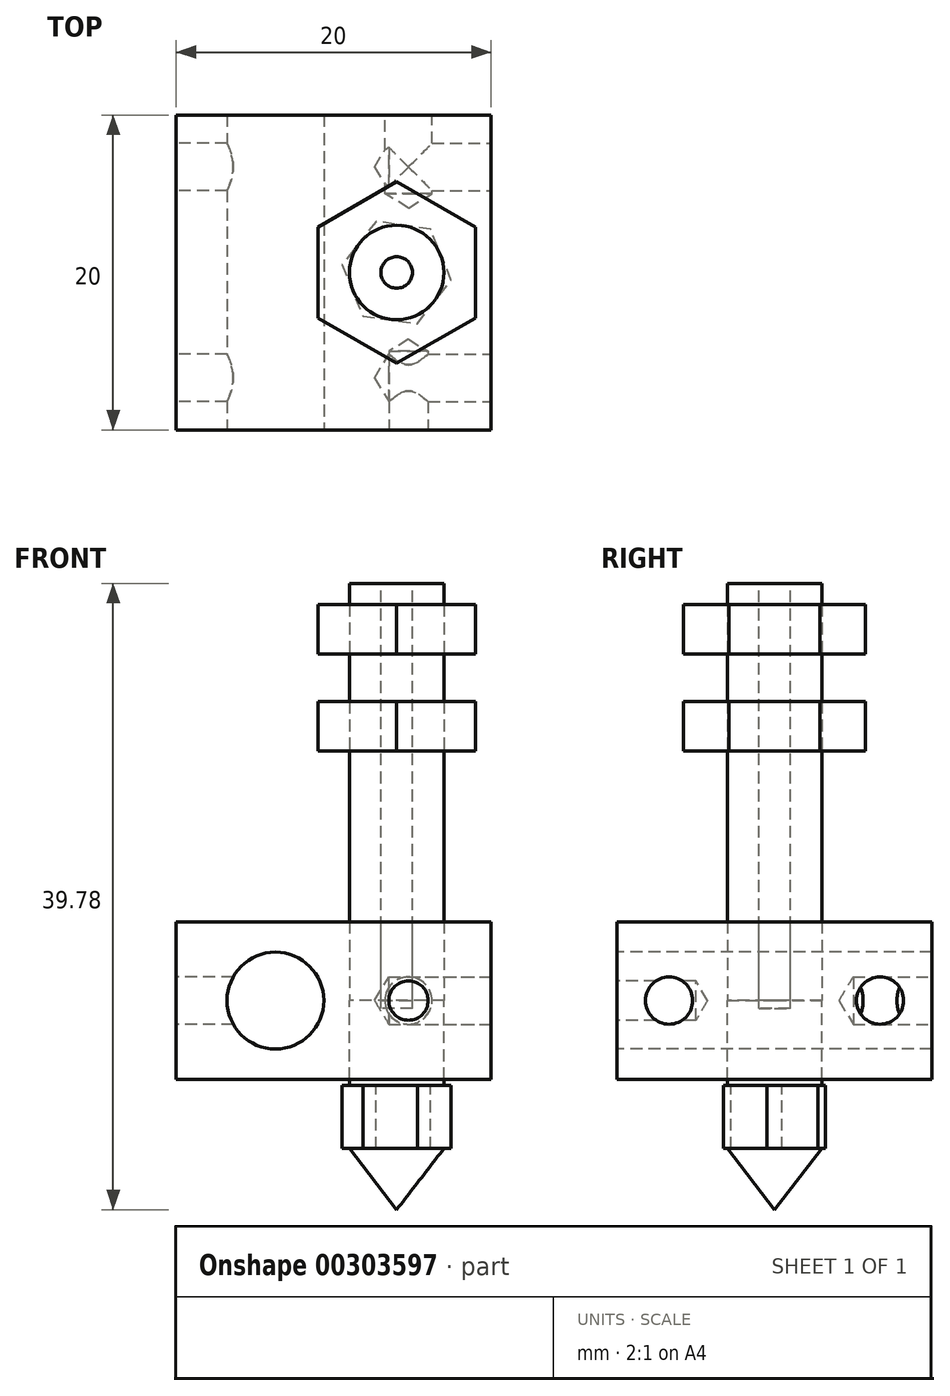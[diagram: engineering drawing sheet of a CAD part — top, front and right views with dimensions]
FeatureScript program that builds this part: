
annotation { "Feature Type Name" : "Feature", "Feature Type Description" : "" }
export const myFeature = defineFeature(function(context is Context, id is Id, definition is map)
    precondition{}
    {
        {
            var Q0;
            Q0=qCreatedBy(makeId("Top.planeOp"),FACE);
            var sketch = newSketch(context, id + "F0", { "sketchPlane" : qUnion([Q0])});
            skCircle(sketch, "E0", {"center": v(0, 0) * mm, "radius": 3 * mm});
            skSolve(sketch);
        }
        {
            var Q0;
            Q0 = qSketchRegion(id + "F0", true);
            extrude(context, id + "F1", {"entities" : qUnion([Q0]), "depth" : 26.5 * mm});
        }
        {
            var Q0;
            Q0=makeQuery(id+"F1.opExtrude","CAP_FACE",FACE,{"disambiguationData":[OSD([sQuery(id+"F0.wireOp",EDGE,"E0")])],"isStart":true});
            var sketch = newSketch(context, id + "F2", { "sketchPlane" : qUnion([Q0])});
            skCircle(sketch, "E1", {"center": v(0, 0) * mm, "radius": 3 * mm});
            skSolve(sketch);
        }
        {
            var Q0;
            Q0 = qSketchRegion(id + "F2", true);
            extrude(context, id + "F3", {"entities" : qUnion([Q0]), "depth" : 5.4 * mm});
        }
        {
            var Q0;
            Q0=makeQuery(id+"F3.opExtrude","CAP_FACE",FACE,{"disambiguationData":[OSD([sQuery(id+"F2.wireOp",EDGE,"E1")])],"isStart":false});
            var sketch = newSketch(context, id + "F4", { "sketchPlane" : qUnion([Q0])});
            skLineSegment(sketch, "E2.0", {"start": v(2.15, -2.76) * mm, "end": v(-1.31, -3.24) * mm});
            skLineSegment(sketch, "E2.1", {"start": v(-1.31, -3.24) * mm, "end": v(-3.46, -0.48) * mm});
            skLineSegment(sketch, "E2.2", {"start": v(-3.46, -0.48) * mm, "end": v(-2.15, 2.76) * mm});
            skLineSegment(sketch, "E2.3", {"start": v(-2.15, 2.76) * mm, "end": v(1.31, 3.24) * mm});
            skLineSegment(sketch, "E2.4", {"start": v(1.31, 3.24) * mm, "end": v(3.46, 0.48) * mm});
            skLineSegment(sketch, "E2.5", {"start": v(3.46, 0.48) * mm, "end": v(2.15, -2.76) * mm});
            skPoint(sketch, "E2.0.midPoint", {"position": v(0.42, -3) * mm});
            skPoint(sketch, "E2.cCircle.center.orphan", {"position": v(0, 0) * mm});
            skSolve(sketch);
        }
        {
            var Q0;
            Q0 = qSketchRegion(id + "F4", true);
            extrude(context, id + "F5", {"entities" : qUnion([Q0]), "operationType" : NewBodyOperationType.ADD, "depth" : 4 * mm});
        }
        {
            var Q0;
            Q0=qCreatedBy(makeId("Front.planeOp"),FACE);
            var sketch = newSketch(context, id + "F6", { "sketchPlane" : qUnion([Q0])});
            skLineSegment(sketch, "E3", {"start": v(0, -9.38) * mm, "end": v(0, -13.28) * mm});
            skLineSegment(sketch, "E4", {"start": v(0, -9.38) * mm, "end": v(-3.01, -9.38) * mm});
            skLineSegment(sketch, "E5", {"start": v(-3.01, -9.38) * mm, "end": v(0, -13.28) * mm});
            skSolve(sketch);
        }
        {
            var Q0;
            Q0 = qSketchRegion(id + "F6", true);
            var Q1;
            Q1=makeQuery(id+"F3.opExtrude","SWEPT_FACE",FACE,{"disambiguationData":[OSD([sQuery(id+"F2.wireOp",EDGE,"E1")])]});
            revolve(context, id + "F7", {"operationType" : NewBodyOperationType.ADD, "entities" : qUnion([Q0]), "axis" : qUnion([Q1]), "revolveType" : RevolveType.FULL});
        }
        {
            var Q0;
            Q0=qCreatedBy(makeId("Top.planeOp"),FACE);
            var sketch = newSketch(context, id + "F8", { "sketchPlane" : qUnion([Q0])});
            skLineSegment(sketch, "E6.bottom", {"start": v(-14, 10) * mm, "end": v(6, 10) * mm});
            skLineSegment(sketch, "E6.top", {"start": v(-14, -10) * mm, "end": v(6, -10) * mm});
            skLineSegment(sketch, "E6.left", {"start": v(-14, 10) * mm, "end": v(-14, -10) * mm});
            skLineSegment(sketch, "E6.right", {"start": v(6, 10) * mm, "end": v(6, -10) * mm});
            skSolve(sketch);
        }
        {
            var Q0;
            Q0 = qSketchRegion(id + "F8", true);
            extrude(context, id + "F9", {"entities" : qUnion([Q0]), "endBound" : BoundingType.SYMMETRIC, "depth" : 10 * mm});
        }
        {
            var Q0;
            Q0=makeQuery(id+"F9.opExtrude","SWEPT_FACE",FACE,{"disambiguationData":[OSD([sQuery(id+"F8.wireOp",EDGE,"E6.top")])]});
            var sketch = newSketch(context, id + "F10", { "sketchPlane" : qUnion([Q0])});
            skPoint(sketch, "E7", {"position": v(0.75, 0) * mm});
            skPoint(sketch, "E8", {"position": v(-7.7, 0) * mm});
            skSolve(sketch);
        }
        {
            var Q0;
            Q0=sQuery(id+"F10.wireOp",VERTEX,"E7");
            var Q1;
            Q1=makeQuery(id+"F9.opExtrude","SWEPT_BODY",BODY,{"disambiguationData":[OSD([sQuery(id+"F8.wireOp",EDGE,"E6.bottom"),sQuery(id+"F8.wireOp",EDGE,"E6.top"),sQuery(id+"F8.wireOp",EDGE,"E6.left"),sQuery(id+"F8.wireOp",EDGE,"E6.right")])]});
            hole(context, id + "F11", {"style" : HoleStyle.SIMPLE, "endStyle" : HoleEndStyle.BLIND, "holeDiameter" : 2.5 * mm, "holeDepth" : 5 * mm, "tappedDepth" : 12 * mm, "tapClearance" : 3, "locations" : qUnion([Q0]), "scope" : qUnion([Q1])});
        }
        {
            var Q0;
            Q0=sQuery(id+"F10.wireOp",VERTEX,"E8");
            var Q1;
            Q1=makeQuery(id+"F9.opExtrude","SWEPT_BODY",BODY,{"disambiguationData":[OSD([sQuery(id+"F8.wireOp",EDGE,"E6.bottom"),sQuery(id+"F8.wireOp",EDGE,"E6.top"),sQuery(id+"F8.wireOp",EDGE,"E6.left"),sQuery(id+"F8.wireOp",EDGE,"E6.right")])]});
            hole(context, id + "F12", {"style" : HoleStyle.SIMPLE, "endStyle" : HoleEndStyle.THROUGH, "holeDiameter" : 6.15 * mm, "tappedDepth" : 12 * mm, "tapClearance" : 3, "locations" : qUnion([Q0]), "scope" : qUnion([Q1])});
        }
        {
            var Q0;
            Q0=makeQuery(id+"F9.opExtrude","SWEPT_FACE",FACE,{"disambiguationData":[OSD([sQuery(id+"F8.wireOp",EDGE,"E6.right")])]});
            var sketch = newSketch(context, id + "F13", { "sketchPlane" : qUnion([Q0])});
            skPoint(sketch, "E9", {"position": v(-6.7, 0) * mm});
            skPoint(sketch, "E9.positionSnap0", {"position": v(-10, 0) * mm});
            skPoint(sketch, "E10", {"position": v(6.7, 0) * mm});
            skSolve(sketch);
        }
        {
            var Q0;
            Q0=sQuery(id+"F13.wireOp",VERTEX,"E9");
            var Q1;
            Q1=sQuery(id+"F13.wireOp",VERTEX,"E10");
            var Q2;
            Q2=makeQuery(id+"F9.opExtrude","SWEPT_BODY",BODY,{"disambiguationData":[OSD([sQuery(id+"F8.wireOp",EDGE,"E6.bottom"),sQuery(id+"F8.wireOp",EDGE,"E6.top"),sQuery(id+"F8.wireOp",EDGE,"E6.left"),sQuery(id+"F8.wireOp",EDGE,"E6.right")])]});
            hole(context, id + "F14", {"style" : HoleStyle.SIMPLE, "endStyle" : HoleEndStyle.BLIND, "holeDiameter" : 3 * mm, "holeDepth" : 6.5 * mm, "tappedDepth" : 12 * mm, "tapClearance" : 3, "locations" : qUnion([Q0, Q1]), "scope" : qUnion([Q2])});
        }
        {
            var Q0;
            Q0=makeQuery(id+"F9.opExtrude","SWEPT_FACE",FACE,{"disambiguationData":[OSD([sQuery(id+"F8.wireOp",EDGE,"E6.bottom")])]});
            var sketch = newSketch(context, id + "F15", { "sketchPlane" : qUnion([Q0])});
            skPoint(sketch, "E11.0", {"position": v(-0.75, 0) * mm});
            skSolve(sketch);
        }
        {
            var Q0;
            Q0=sQuery(id+"F15.wireOp",VERTEX,"E11.0");
            var Q1;
            Q1=makeQuery(id+"F9.opExtrude","SWEPT_BODY",BODY,{"disambiguationData":[OSD([sQuery(id+"F8.wireOp",EDGE,"E6.bottom"),sQuery(id+"F8.wireOp",EDGE,"E6.top"),sQuery(id+"F8.wireOp",EDGE,"E6.left"),sQuery(id+"F8.wireOp",EDGE,"E6.right")])]});
            hole(context, id + "F16", {"style" : HoleStyle.SIMPLE, "endStyle" : HoleEndStyle.BLIND, "holeDiameter" : 3 * mm, "holeDepth" : 5 * mm, "tappedDepth" : 12 * mm, "tapClearance" : 3, "locations" : qUnion([Q0]), "scope" : qUnion([Q1])});
        }
        {
            var Q0;
            Q0=makeQuery(id+"F9.opExtrude","SWEPT_FACE",FACE,{"disambiguationData":[OSD([sQuery(id+"F8.wireOp",EDGE,"E6.left")])]});
            var sketch = newSketch(context, id + "F17", { "sketchPlane" : qUnion([Q0])});
            skPoint(sketch, "E12.0", {"position": v(-6.7, 0) * mm});
            skPoint(sketch, "E12.1", {"position": v(6.7, 0) * mm});
            skSolve(sketch);
        }
        {
            var Q0;
            Q0=sQuery(id+"F17.wireOp",VERTEX,"E12.0");
            var Q1;
            Q1=sQuery(id+"F17.wireOp",VERTEX,"E12.1");
            var Q2;
            Q2=makeQuery(id+"F9.opExtrude","SWEPT_BODY",BODY,{"disambiguationData":[OSD([sQuery(id+"F8.wireOp",EDGE,"E6.bottom"),sQuery(id+"F8.wireOp",EDGE,"E6.top"),sQuery(id+"F8.wireOp",EDGE,"E6.left"),sQuery(id+"F8.wireOp",EDGE,"E6.right")])]});
            hole(context, id + "F18", {"style" : HoleStyle.SIMPLE, "endStyle" : HoleEndStyle.BLIND, "holeDiameter" : 3 * mm, "holeDepth" : 6.5 * mm, "tappedDepth" : 12 * mm, "tapClearance" : 3, "locations" : qUnion([Q0, Q1]), "scope" : qUnion([Q2])});
        }
        {
            var Q0;
            Q0=makeQuery(id+"F1.opExtrude","CAP_FACE",FACE,{"disambiguationData":[OSD([sQuery(id+"F0.wireOp",EDGE,"E0")])],"isStart":false});
            var sketch = newSketch(context, id + "F19", { "sketchPlane" : qUnion([Q0])});
            skCircle(sketch, "E13", {"center": v(0, 0) * mm, "radius": 1 * mm});
            skSolve(sketch);
        }
        {
            var Q0;
            Q0=makeQuery(id+"F19.imprint","IMPRINT",FACE,{"disambiguationData":[TD([[makeQuery(id+"F19.imprint","IMPRINT",EDGE,{"derivedFrom":sQuery(id+"F19.wireOp",EDGE,"E13")}),1.0]])]});
            var Q1;
            Q1=sQuery(id+"F19.wireOp",EDGE,"E13");
            extrude(context, id + "F20", {"entities" : qUnion([Q0]), "operationType" : NewBodyOperationType.REMOVE, "surfaceEntities" : qUnion([Q1]), "oppositeDirection" : true, "depth" : 27 * mm});
        }
        {
            var Q0;
            Q0=makeQuery(id+"F1.opExtrude","CAP_FACE",FACE,{"disambiguationData":[OSD([sQuery(id+"F0.wireOp",EDGE,"E0")])],"isStart":false});
            var sketch = newSketch(context, id + "F21", { "sketchPlane" : qUnion([Q0])});
            skCircle(sketch, "E14.cCircle", {"center": v(0, 0) * mm, "radius": 5 * mm, "construction": true});
            skLineSegment(sketch, "E14.0", {"start": v(5, 2.89) * mm, "end": v(5, -2.89) * mm});
            skLineSegment(sketch, "E14.1", {"start": v(5, -2.89) * mm, "end": v(0, -5.77) * mm});
            skLineSegment(sketch, "E14.2", {"start": v(0, -5.77) * mm, "end": v(-5, -2.89) * mm});
            skLineSegment(sketch, "E14.3", {"start": v(-5, -2.89) * mm, "end": v(-5, 2.89) * mm});
            skLineSegment(sketch, "E14.4", {"start": v(-5, 2.89) * mm, "end": v(0, 5.77) * mm});
            skLineSegment(sketch, "E14.5", {"start": v(0, 5.77) * mm, "end": v(5, 2.89) * mm});
            skPoint(sketch, "E14.0.midPoint", {"position": v(5, 0) * mm});
            skCircle(sketch, "E15", {"center": v(0, 0) * mm, "radius": 3 * mm});
            skSolve(sketch);
        }
        {
            var Q0;
            Q0 = qSketchRegion(id + "F21", true);
            extrude(context, id + "F22", {"entities" : qUnion([Q0]), "depth" : 3.15 * mm});
        }
        {
            var Q0;
            Q0=makeQuery(id+"F22.opExtrude","SWEPT_BODY",BODY,{"disambiguationData":[OSD([sQuery(id+"F21.wireOp",EDGE,"E14.0"),sQuery(id+"F21.wireOp",EDGE,"E14.1"),sQuery(id+"F21.wireOp",EDGE,"E14.2"),sQuery(id+"F21.wireOp",EDGE,"E14.3"),sQuery(id+"F21.wireOp",EDGE,"E14.4"),sQuery(id+"F21.wireOp",EDGE,"E14.5"),sQuery(id+"F21.wireOp",EDGE,"E15")])]});
            transform(context, id + "F23", {"entities" : qUnion([Q0]), "transformType" : TransformType.TRANSLATION_3D, "dx" : 0 * mm, "dy" : 0 * mm, "dz" : -4.5 * mm, "makeCopy" : false});
        }
        {
            var Q0;
            Q0=makeQuery(id+"F22.opExtrude","SWEPT_BODY",BODY,{"disambiguationData":[OSD([sQuery(id+"F21.wireOp",EDGE,"E14.0"),sQuery(id+"F21.wireOp",EDGE,"E14.1"),sQuery(id+"F21.wireOp",EDGE,"E14.2"),sQuery(id+"F21.wireOp",EDGE,"E14.3"),sQuery(id+"F21.wireOp",EDGE,"E14.4"),sQuery(id+"F21.wireOp",EDGE,"E14.5"),sQuery(id+"F21.wireOp",EDGE,"E15")])]});
            transform(context, id + "F24", {"entities" : qUnion([Q0]), "transformType" : TransformType.TRANSLATION_3D, "dx" : 0 * mm, "dy" : 0 * mm, "dz" : -6.15 * mm, "makeCopy" : true});
        }
    });
